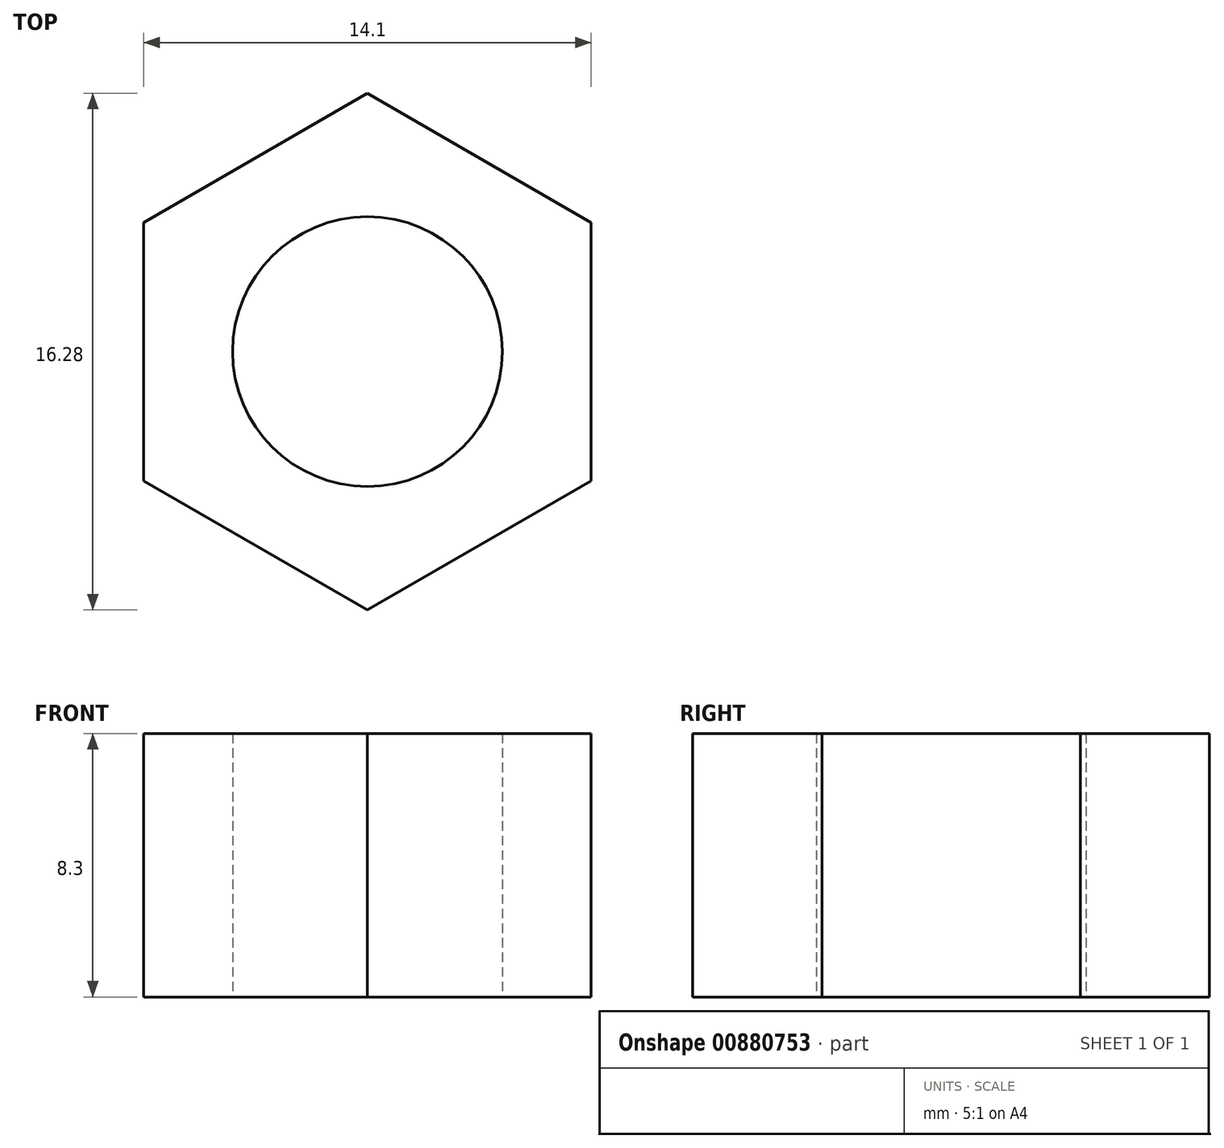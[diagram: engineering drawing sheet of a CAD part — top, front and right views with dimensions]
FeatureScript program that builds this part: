
annotation { "Feature Type Name" : "Feature", "Feature Type Description" : "" }
export const myFeature = defineFeature(function(context is Context, id is Id, definition is map)
    precondition{}
    {
        {
            assignVariable(context, id + "F0", {"name" : "height", "anyValue" : 8.3});
        }
        {
            var Q0;
            Q0=qCreatedBy(makeId("Top.planeOp"),FACE);
            var sketch = newSketch(context, id + "F1", { "sketchPlane" : qUnion([Q0])});
            skCircle(sketch, "E0.cCircle", {"center": v(0, 0) * mm, "radius": 7.05 * mm, "construction": true});
            skLineSegment(sketch, "E0.0", {"start": v(-7.05, -4.07) * mm, "end": v(-7.05, 4.07) * mm});
            skLineSegment(sketch, "E0.1", {"start": v(-7.05, 4.07) * mm, "end": v(0, 8.14) * mm});
            skLineSegment(sketch, "E0.2", {"start": v(0, 8.14) * mm, "end": v(7.05, 4.07) * mm});
            skLineSegment(sketch, "E0.3", {"start": v(7.05, 4.07) * mm, "end": v(7.05, -4.07) * mm});
            skLineSegment(sketch, "E0.4", {"start": v(7.05, -4.07) * mm, "end": v(0, -8.14) * mm});
            skLineSegment(sketch, "E0.5", {"start": v(0, -8.14) * mm, "end": v(-7.05, -4.07) * mm});
            skPoint(sketch, "E0.0.midPoint", {"position": v(-7.05, 0) * mm});
            skCircle(sketch, "E1", {"center": v(0, 0) * mm, "radius": 4.25 * mm});
            skSolve(sketch);
        }
        {
            var Q0;
            Q0=makeQuery(id+"F1.imprint","IMPRINT",FACE,{"disambiguationData":[TD([[makeQuery(id+"F1.imprint","IMPRINT",EDGE,{"derivedFrom":sQuery(id+"F1.wireOp",EDGE,"E0.0")}),-1.0]])]});
            extrude(context, id + "F2", {"entities" : qUnion([Q0]), "depth" : (getVariable(context, 'height')) * mm, "offsetDistance" : 25 * mm});
        }
    });
